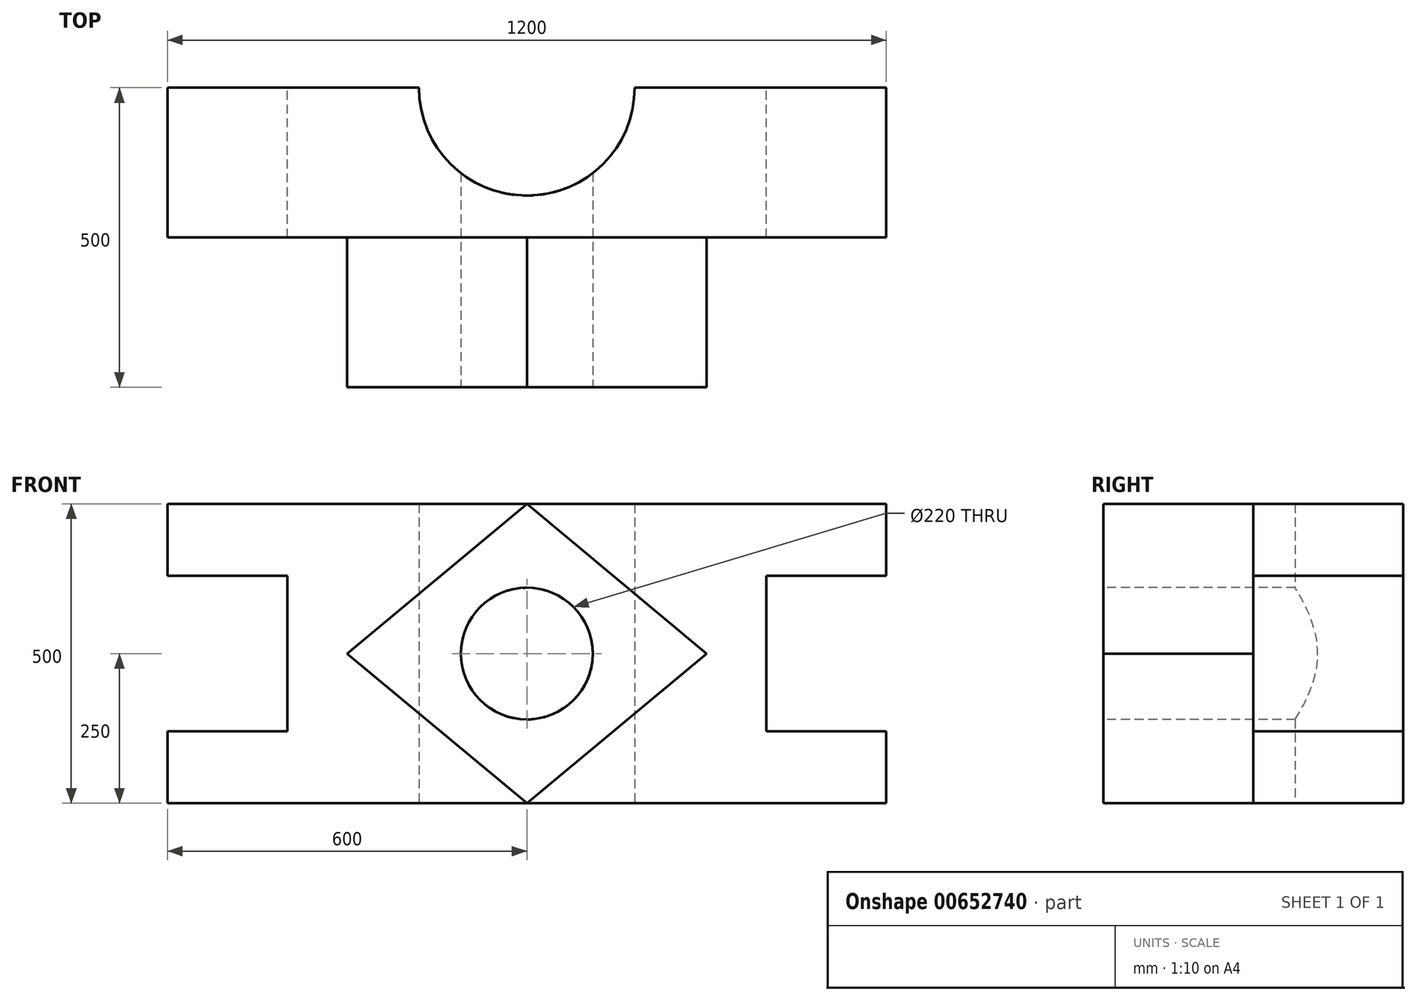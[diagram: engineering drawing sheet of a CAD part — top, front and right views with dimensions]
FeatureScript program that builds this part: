
annotation { "Feature Type Name" : "Feature", "Feature Type Description" : "" }
export const myFeature = defineFeature(function(context is Context, id is Id, definition is map)
    precondition{}
    {
        {
            var Q0;
            Q0=qCreatedBy(makeId("Front.planeOp"),FACE);
            var sketch = newSketch(context, id + "F0", { "sketchPlane" : qUnion([Q0])});
            skLineSegment(sketch, "E0.bottom", {"start": v(-600, -250) * mm, "end": v(600, -250) * mm});
            skLineSegment(sketch, "E0.top", {"start": v(-600, 250) * mm, "end": v(600, 250) * mm});
            skLineSegment(sketch, "E0.left", {"start": v(-600, -250) * mm, "end": v(-600, 250) * mm});
            skLineSegment(sketch, "E0.right", {"start": v(600, -250) * mm, "end": v(600, 250) * mm});
            skPoint(sketch, "E0.middle", {"position": v(0, 0) * mm});
            skPoint(sketch, "E1.middle", {"position": v(-600, 0) * mm});
            skPoint(sketch, "E2.middle", {"position": v(600, 0) * mm});
            skSolve(sketch);
        }
        {
            var Q0;
            Q0 = qSketchRegion(id + "F0", true);
            extrude(context, id + "F1", {"entities" : qUnion([Q0]), "depth" : 250 * mm, "offsetDistance" : 25 * mm});
        }
        {
            var Q0;
            Q0=makeQuery(id+"F1.opExtrude","CAP_FACE",FACE,{"disambiguationData":[OSD([sQuery(id+"F0.wireOp",EDGE,"E0.bottom"),sQuery(id+"F0.wireOp",EDGE,"E0.top"),sQuery(id+"F0.wireOp",EDGE,"E0.left"),sQuery(id+"F0.wireOp",EDGE,"E0.right")])],"isStart":true});
            var sketch = newSketch(context, id + "F2", { "sketchPlane" : qUnion([Q0])});
            skLineSegment(sketch, "E3.bottom", {"start": v(-800, -130) * mm, "end": v(-400, -130) * mm});
            skLineSegment(sketch, "E3.top", {"start": v(-800, 130) * mm, "end": v(-400, 130) * mm});
            skLineSegment(sketch, "E3.left", {"start": v(-800, -130) * mm, "end": v(-800, 130) * mm});
            skLineSegment(sketch, "E3.right", {"start": v(-400, -130) * mm, "end": v(-400, 130) * mm});
            skPoint(sketch, "E3.middle", {"position": v(-600, 0) * mm});
            skLineSegment(sketch, "E4.bottom", {"start": v(400, -130) * mm, "end": v(800, -130) * mm});
            skLineSegment(sketch, "E4.top", {"start": v(400, 130) * mm, "end": v(800, 130) * mm});
            skLineSegment(sketch, "E4.left", {"start": v(400, -130) * mm, "end": v(400, 130) * mm});
            skLineSegment(sketch, "E4.right", {"start": v(800, -130) * mm, "end": v(800, 130) * mm});
            skPoint(sketch, "E4.middle", {"position": v(600, 0) * mm});
            skSolve(sketch);
        }
        {
            var Q0;
            Q0 = qSketchRegion(id + "F2", true);
            extrude(context, id + "F3", {"entities" : qUnion([Q0]), "operationType" : NewBodyOperationType.REMOVE, "endBound" : BoundingType.THROUGH_ALL, "oppositeDirection" : true, "depth" : 25 * mm, "offsetDistance" : 25 * mm});
        }
        {
            var Q0;
            Q0=makeQuery(id+"F1.opExtrude","CAP_FACE",FACE,{"disambiguationData":[OSD([sQuery(id+"F0.wireOp",EDGE,"E0.bottom"),sQuery(id+"F0.wireOp",EDGE,"E0.top"),sQuery(id+"F0.wireOp",EDGE,"E0.left"),sQuery(id+"F0.wireOp",EDGE,"E0.right")])],"isStart":false});
            var sketch = newSketch(context, id + "F4", { "sketchPlane" : qUnion([Q0])});
            skPoint(sketch, "E5.middle", {"position": v(0, 0) * mm});
            skLineSegment(sketch, "E6", {"start": v(-300, 0) * mm, "end": v(0, -250) * mm});
            skLineSegment(sketch, "E7", {"start": v(0, -250) * mm, "end": v(300, 0) * mm});
            skLineSegment(sketch, "E8", {"start": v(300, 0) * mm, "end": v(0, 250) * mm});
            skLineSegment(sketch, "E9", {"start": v(0, 250) * mm, "end": v(-300, 0) * mm});
            skSolve(sketch);
        }
        {
            var Q0;
            Q0 = qSketchRegion(id + "F4", true);
            extrude(context, id + "F5", {"entities" : qUnion([Q0]), "operationType" : NewBodyOperationType.ADD, "depth" : 250 * mm, "offsetDistance" : 25 * mm});
        }
        {
            var Q0;
            Q0=makeQuery(id+"F5.opExtrude","CAP_FACE",FACE,{"disambiguationData":[OSD([sQuery(id+"F4.wireOp",EDGE,"E6"),sQuery(id+"F4.wireOp",EDGE,"E7"),sQuery(id+"F4.wireOp",EDGE,"E8"),sQuery(id+"F4.wireOp",EDGE,"E9")])],"isStart":false});
            var sketch = newSketch(context, id + "F6", { "sketchPlane" : qUnion([Q0])});
            skCircle(sketch, "E10", {"center": v(0, 0) * mm, "radius": 110 * mm});
            skSolve(sketch);
        }
        {
            var Q0;
            Q0 = qSketchRegion(id + "F6", true);
            extrude(context, id + "F7", {"entities" : qUnion([Q0]), "operationType" : NewBodyOperationType.REMOVE, "endBound" : BoundingType.THROUGH_ALL, "oppositeDirection" : true, "depth" : 25 * mm, "offsetDistance" : 25 * mm});
        }
        {
            var Q0;
            Q0=makeQuery(id+"F1.opExtrude","SWEPT_FACE",FACE,{"disambiguationData":[OSD([sQuery(id+"F0.wireOp",EDGE,"E0.bottom")])]});
            var sketch = newSketch(context, id + "F8", { "sketchPlane" : qUnion([Q0])});
            skCircle(sketch, "E11", {"center": v(0, 0) * mm, "radius": 180 * mm});
            skSolve(sketch);
        }
        {
            var Q0;
            Q0 = qSketchRegion(id + "F8", true);
            extrude(context, id + "F9", {"entities" : qUnion([Q0]), "operationType" : NewBodyOperationType.REMOVE, "endBound" : BoundingType.THROUGH_ALL, "oppositeDirection" : true, "depth" : 25 * mm, "offsetDistance" : 25 * mm});
        }
    });
